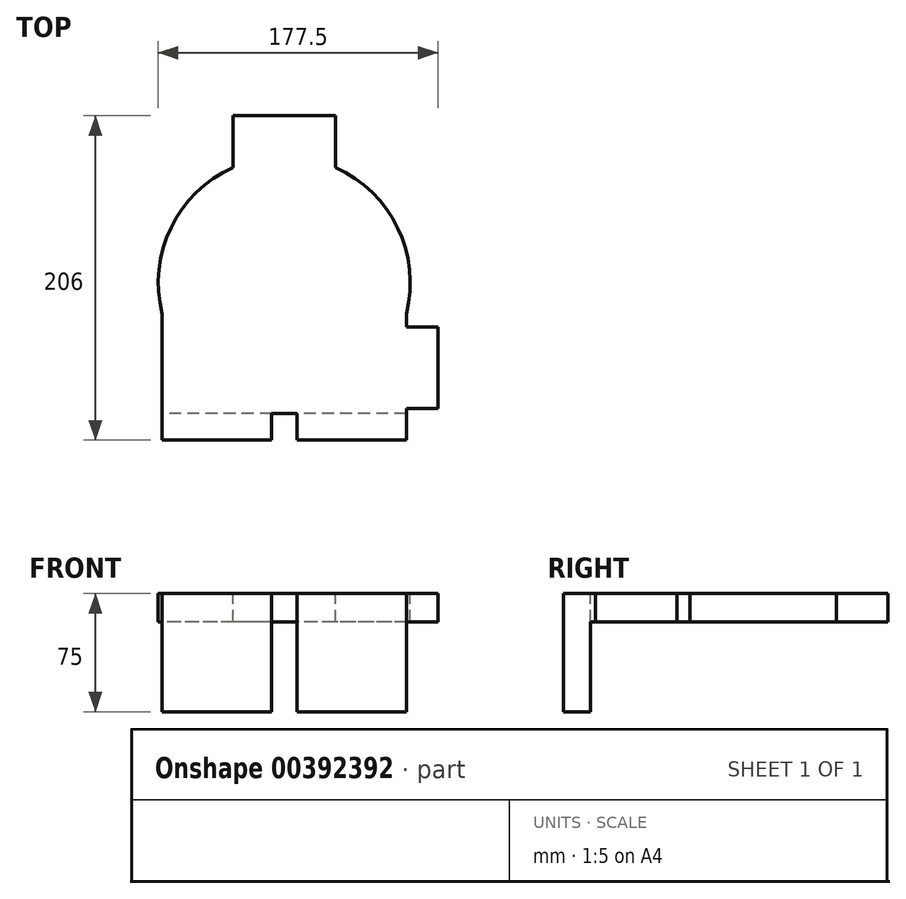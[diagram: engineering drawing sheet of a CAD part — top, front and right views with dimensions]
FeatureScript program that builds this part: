
annotation { "Feature Type Name" : "Feature", "Feature Type Description" : "" }
export const myFeature = defineFeature(function(context is Context, id is Id, definition is map)
    precondition{}
    {
        {
            var Q0;
            Q0=qCreatedBy(makeId("Top.planeOp"),FACE);
            var sketch = newSketch(context, id + "F0", { "sketchPlane" : qUnion([Q0])});
            skLineSegment(sketch, "E0.top", {"start": v(-77.5, -100) * mm, "end": v(77.5, -100) * mm});
            skLineSegment(sketch, "E0.left", {"start": v(-77.5, -19.84) * mm, "end": v(-77.5, -100) * mm});
            skLineSegment(sketch, "E0.right", {"start": v(77.5, -19.84) * mm, "end": v(77.5, -28) * mm});
            skPoint(sketch, "E1", {"position": v(0, 0) * mm});
            skLineSegment(sketch, "E2.bottom", {"start": v(77.5, -80) * mm, "end": v(97.5, -80) * mm});
            skLineSegment(sketch, "E2.top", {"start": v(77.5, -28) * mm, "end": v(97.5, -28) * mm});
            skLineSegment(sketch, "E2.right", {"start": v(97.5, -80) * mm, "end": v(97.5, -28) * mm});
            skLineSegment(sketch, "E3.bottom", {"start": v(-8, -100) * mm, "end": v(8, -100) * mm});
            skLineSegment(sketch, "E3.top", {"start": v(-8, -55) * mm, "end": v(8, -55) * mm});
            skLineSegment(sketch, "E3.left", {"start": v(-8, -100) * mm, "end": v(-8, -55) * mm});
            skLineSegment(sketch, "E3.right", {"start": v(8, -100) * mm, "end": v(8, -55) * mm});
            skPoint(sketch, "E4", {"position": v(0, -100) * mm});
            skPoint(sketch, "E5", {"position": v(0, -55) * mm});
            skLineSegment(sketch, "E6.bottom", {"start": v(22, -55) * mm, "end": v(-22, -55) * mm});
            skLineSegment(sketch, "E6.top", {"start": v(22, -39) * mm, "end": v(-22, -39) * mm});
            skLineSegment(sketch, "E6.left", {"start": v(30, -47) * mm, "end": v(30, -47) * mm});
            skLineSegment(sketch, "E6.right", {"start": v(-30, -47) * mm, "end": v(-30, -47) * mm});
            skPoint(sketch, "E6.middle", {"position": v(0, -47) * mm});
            skPoint(sketch, "E7.visualSharp", {"position": v(-30, -39) * mm});
            skArc(sketch, "E7.filletArc", {"start": v(-22, -39) * mm, "mid": v(-27.66, -41.34) * mm, "end": v(-30, -47) * mm});
            skPoint(sketch, "E8.visualSharp", {"position": v(-30, -55) * mm});
            skArc(sketch, "E8.filletArc", {"start": v(-30, -47) * mm, "mid": v(-27.66, -52.66) * mm, "end": v(-22, -55) * mm});
            skPoint(sketch, "E9.visualSharp", {"position": v(30, -55) * mm});
            skArc(sketch, "E9.filletArc", {"start": v(22, -55) * mm, "mid": v(27.66, -52.66) * mm, "end": v(30, -47) * mm});
            skPoint(sketch, "E10.visualSharp", {"position": v(30, -39) * mm});
            skArc(sketch, "E10.filletArc", {"start": v(30, -47) * mm, "mid": v(27.66, -41.34) * mm, "end": v(22, -39) * mm});
            skArc(sketch, "E11", {"start": v(77.5, -19.84) * mm, "mid": v(72, 34.86) * mm, "end": v(32.5, 73.1) * mm});
            skLineSegment(sketch, "E12.trimOffspring", {"start": v(77.5, -80) * mm, "end": v(77.5, -100) * mm});
            skLineSegment(sketch, "E13.bottom", {"start": v(32.5, 106) * mm, "end": v(-32.5, 106) * mm});
            skLineSegment(sketch, "E13.left", {"start": v(32.5, 106) * mm, "end": v(32.5, 73.1) * mm});
            skLineSegment(sketch, "E13.right", {"start": v(-32.5, 106) * mm, "end": v(-32.5, 73.1) * mm});
            skArc(sketch, "E14.trimOffspring", {"start": v(-32.5, 73.1) * mm, "mid": v(-72, 34.86) * mm, "end": v(-77.5, -19.84) * mm});
            skLineSegment(sketch, "E15.top", {"start": v(0, 46) * mm, "end": v(0, 46) * mm});
            skLineSegment(sketch, "E15.left", {"start": v(8, 106) * mm, "end": v(8, 54) * mm});
            skLineSegment(sketch, "E15.right", {"start": v(-8, 106) * mm, "end": v(-8, 54) * mm});
            skPoint(sketch, "E15.middle", {"position": v(0, 106) * mm});
            skPoint(sketch, "E16.visualSharp", {"position": v(-8, 46) * mm});
            skArc(sketch, "E16.filletArc", {"start": v(-8, 54) * mm, "mid": v(-5.66, 48.34) * mm, "end": v(0, 46) * mm});
            skPoint(sketch, "E17.visualSharp", {"position": v(8, 46) * mm});
            skArc(sketch, "E17.filletArc", {"start": v(0, 46) * mm, "mid": v(5.66, 48.34) * mm, "end": v(8, 54) * mm});
            skLineSegment(sketch, "E18", {"start": v(-8, 106) * mm, "end": v(8, 106) * mm, "construction": true});
            skCircle(sketch, "E19", {"center": v(0, 0) * mm, "radius": 32.5 * mm, "construction": true});
            skLineSegment(sketch, "E20", {"start": v(77.5, -83) * mm, "end": v(-77.5, -83) * mm});
            skSolve(sketch);
        }
        {
            var Q0;
            Q0=makeQuery(id+"F0.imprint","IMPRINT",FACE,{"disambiguationData":[TD([[makeQuery(id+"F0.imprint","IMPRINT",EDGE,{"derivedFrom":sQuery(id+"F0.wireOp",EDGE,"E0.right")}),-1.0]])]});
            var Q1;
            {var subQ0=sQuery(id+"F0.wireOp",EDGE,"E6.bottom");var subQ1=sQuery(id+"F0.wireOp",EDGE,"E3.left");var subQ2=makeQuery(id+"F0.imprint","INTERSECT",VERTEX,{"derivedFrom":[subQ1,subQ0]});Q1=makeQuery(id+"F0.imprint","IMPRINT",FACE,{"disambiguationData":[TD([[makeQuery(id+"F0.imprint","IMPRINT",EDGE,{"disambiguationData":[TD([[subQ2,1.0]])],"derivedFrom":subQ1}),-1.0]])]});}
            var Q2;
            Q2=makeQuery(id+"F0.imprint","IMPRINT",FACE,{"disambiguationData":[TD([[makeQuery(id+"F0.imprint","IMPRINT",EDGE,{"derivedFrom":sQuery(id+"F0.wireOp",EDGE,"E6.top")}),1.0]])]});
            var Q3;
            {var subQ1=sQuery(id+"F0.wireOp",EDGE,"E15.left");Q3=makeQuery(id+"F0.imprint","IMPRINT",FACE,{"disambiguationData":[TD([[makeQuery(id+"F0.imprint","IMPRINT",EDGE,{"derivedFrom":subQ1}),-1.0]])]});}
            extrude(context, id + "F1", {"entities" : qUnion([Q0, Q1, Q2, Q3]), "oppositeDirection" : true, "depth" : 18 * mm});
        }
        {
            var Q0;
            {var subQ0=sQuery(id+"F0.wireOp",EDGE,"E12.trimOffspring");var subQ1=sQuery(id+"F0.wireOp",EDGE,"E0.top");var subQ2=makeQuery(id+"F0.imprint","INTERSECT",VERTEX,{"derivedFrom":[subQ1,subQ0]});Q0=makeQuery(id+"F0.imprint","IMPRINT",FACE,{"disambiguationData":[TD([[makeQuery(id+"F0.imprint","IMPRINT",EDGE,{"disambiguationData":[TD([[subQ2,1.0]])],"derivedFrom":subQ0}),-1.0]])]});}
            var Q1;
            {var subQ0=sQuery(id+"F0.wireOp",EDGE,"E3.bottom");Q1=makeQuery(id+"F0.imprint","IMPRINT",FACE,{"disambiguationData":[TD([[makeQuery(id+"F0.imprint","IMPRINT",EDGE,{"derivedFrom":subQ0}),1.0]])]});}
            var Q2;
            {var subQ0=sQuery(id+"F0.wireOp",EDGE,"E0.left");var subQ1=sQuery(id+"F0.wireOp",EDGE,"E0.top");var subQ2=makeQuery(id+"F0.imprint","INTERSECT",VERTEX,{"derivedFrom":[subQ1,subQ0]});Q2=makeQuery(id+"F0.imprint","IMPRINT",FACE,{"disambiguationData":[TD([[makeQuery(id+"F0.imprint","IMPRINT",EDGE,{"disambiguationData":[TD([[subQ2,1.0]])],"derivedFrom":subQ0}),1.0]])]});}
            extrude(context, id + "F2", {"entities" : qUnion([Q0, Q1, Q2]), "operationType" : NewBodyOperationType.ADD, "oppositeDirection" : true, "depth" : 75 * mm});
        }
    });
